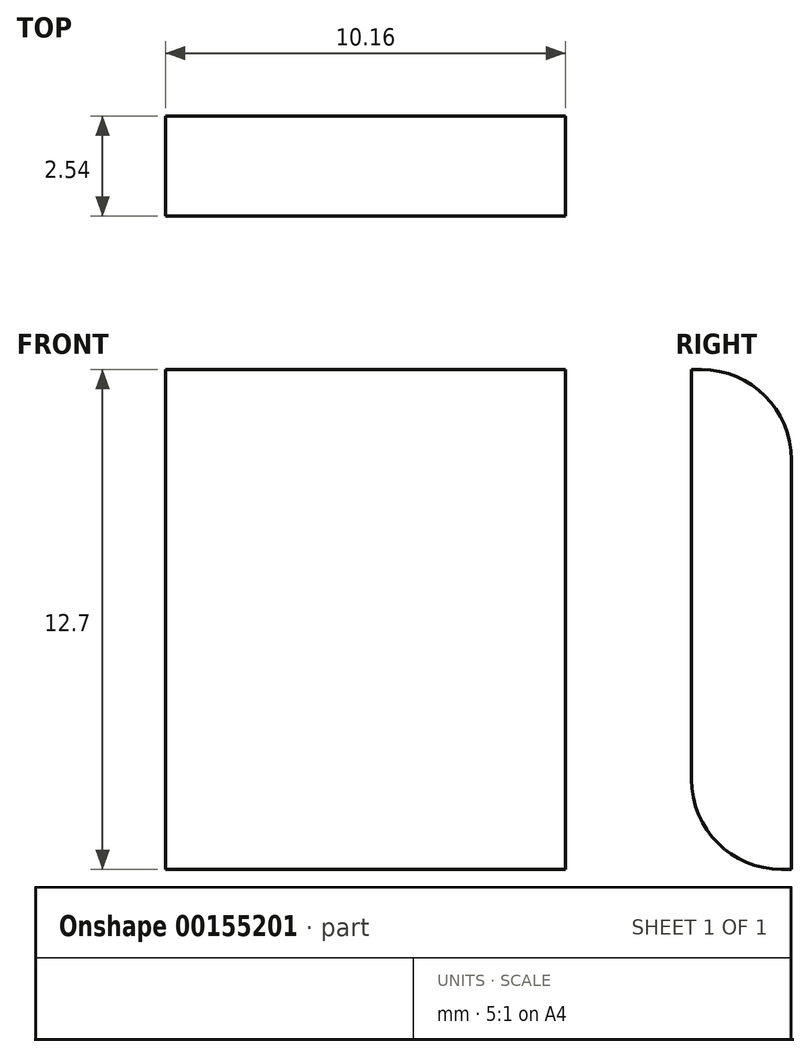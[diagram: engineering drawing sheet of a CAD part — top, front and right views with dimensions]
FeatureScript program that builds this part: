
annotation { "Feature Type Name" : "Feature", "Feature Type Description" : "" }
export const myFeature = defineFeature(function(context is Context, id is Id, definition is map)
    precondition{}
    {
        {
            var Q0;
            Q0=qCreatedBy(makeId("Front.planeOp"),FACE);
            var sketch = newSketch(context, id + "F0", { "sketchPlane" : qUnion([Q0])});
            skLineSegment(sketch, "E0.bottom", {"start": v(5.08, -6.35) * mm, "end": v(-5.08, -6.35) * mm});
            skLineSegment(sketch, "E0.top", {"start": v(5.08, 6.35) * mm, "end": v(-5.08, 6.35) * mm});
            skLineSegment(sketch, "E0.left", {"start": v(5.08, -6.35) * mm, "end": v(5.08, 6.35) * mm});
            skLineSegment(sketch, "E0.right", {"start": v(-5.08, -6.35) * mm, "end": v(-5.08, 6.35) * mm});
            skPoint(sketch, "E0.middle", {"position": v(0, 0) * mm});
            skSolve(sketch);
        }
        {
            var Q0;
            Q0=makeQuery(id+"F0.imprint","IMPRINT",FACE,{"disambiguationData":[TD([[makeQuery(id+"F0.imprint","IMPRINT",EDGE,{"derivedFrom":sQuery(id+"F0.wireOp",EDGE,"E0.bottom")}),-1.0]])]});
            extrude(context, id + "F1", {"entities" : qUnion([Q0]), "depth" : 2.54 * mm});
        }
        {
            var Q0;
            Q0=makeQuery(id+"F1.opExtrude","CAP_EDGE",EDGE,{"disambiguationData":[OSD([sQuery(id+"F0.wireOp",EDGE,"E0.bottom")])],"isStart":false});
            fillet(context, id + "F2", {"entities" : qUnion([Q0]), "radius" : 2.3 * mm, "tangentPropagation" : true, "allowEdgeOverflow" : false});
        }
        {
            var Q0;
            Q0=makeQuery(id+"F1.opExtrude","CAP_EDGE",EDGE,{"disambiguationData":[OSD([sQuery(id+"F0.wireOp",EDGE,"E0.top")])],"isStart":true});
            fillet(context, id + "F3", {"entities" : qUnion([Q0]), "radius" : 2.3 * mm, "tangentPropagation" : true, "allowEdgeOverflow" : false});
        }
    });
